# Revit family: Z-Niederhalter Set für Gleitelemente ab 140 mm Breite
name_source: partatom
category: HLS-Bauteile
revit_build: Autodesk Revit 2017 (Build: 20190507_1515(x64)
units: mm (PartAtom-declared; Revit-internal decimal feet)

## family parameters
Arbeitsebenenbasiert = Ja
Beim Laden mit Abzugskörper schneiden = Nein
Bemaßung runder Anschluss = Durchmesser verwenden
Gemeinsam genutzt = Ja
Immer vertikal = Nein
Raumberechnungspunkt = Nein
Teiletyp = Normal

## types (1)
- Z-Niederhalter Set für Gleitelement ab 140 Breite
    Achsabstand Lochung = 116 mm
    Achsabstand U-Bügel = 116 mm
    Anzahl Befestigungsloch = 2 St
    Artikelnummer = 14799140
    B = 100 mm  [stored 0.328084 ft]
    B1 = 75 mm  [stored 0.246063 ft]
    Breite Z-Niederhalter = 64,5 mm
    D = 11 mm
    EAN = 4250928449443
    Fabrikat = MEFA
    Firma = MEFA Befestigungs- und Montagesysteme GmbH
    Gewicht = 1.09 kg
    Gewicht pro Bauteil = 1.09 kg
    Gewinde = M10
    Gleitreibungsfaktor = 0,15 - 0,25
    H = 31 mm  [stored 0.101706 ft]
    H1 = 100 mm  [stored 0.328084 ft]
    Haftreibungsfaktor = 0,2 - 0,3
    Höhe U-Bügel = 136 mm
    Höhe Z-Niederhalter = 22 mm  [stored 0.0721785 ft]
    Kurztext1 = Z-Niederhalter Set U-Bügel
    Kurztext2 = für Gleitelementbreite ab 140 mm
    L = 150 mm  [stored 0.492126 ft]
    L1 = 116 mm  [stored 0.380577 ft]
    L2 = 80 mm  [stored 0.262467 ft]
    L2 max = 118 mm
    L2 min = 4 mm  [stored 0.0131234 ft]
    Lochdurchmesser = 10.5 mm
    Länge Gewinde = 40 mm  [stored 0.131234 ft]
    Länge Z-Niederhalter = 150 mm  [stored 0.492126 ft]
    MD = 5 mm  [stored 0.0164042 ft]
    Material = Stahl
    Materialname = S235
    Mengeneinheit = SET
    Oberflaeche = Zink-Nickel
    Stärke = 3 mm  [stored 0.00984252 ft]
    Vorgabe-Ansicht = 1219 mm
    für Gleitelementbreite = ab 140 mm
    für Profil = 100 x 100 mm
    für max. Plattenstärke = 16 mm
    max. Temperaturbeständigkeit = 110 °C
    max. zul. Abhebelast (Paar) = 4.50 kN
    vpe = 1 SET

note: [stored X ft] marks values corroborated as IEEE doubles in the binary element streams (Revit-internal decimal feet)

## geometry (parser evidence)
native form markers: Sweep x3
no freeform markers — native parametric forms only
